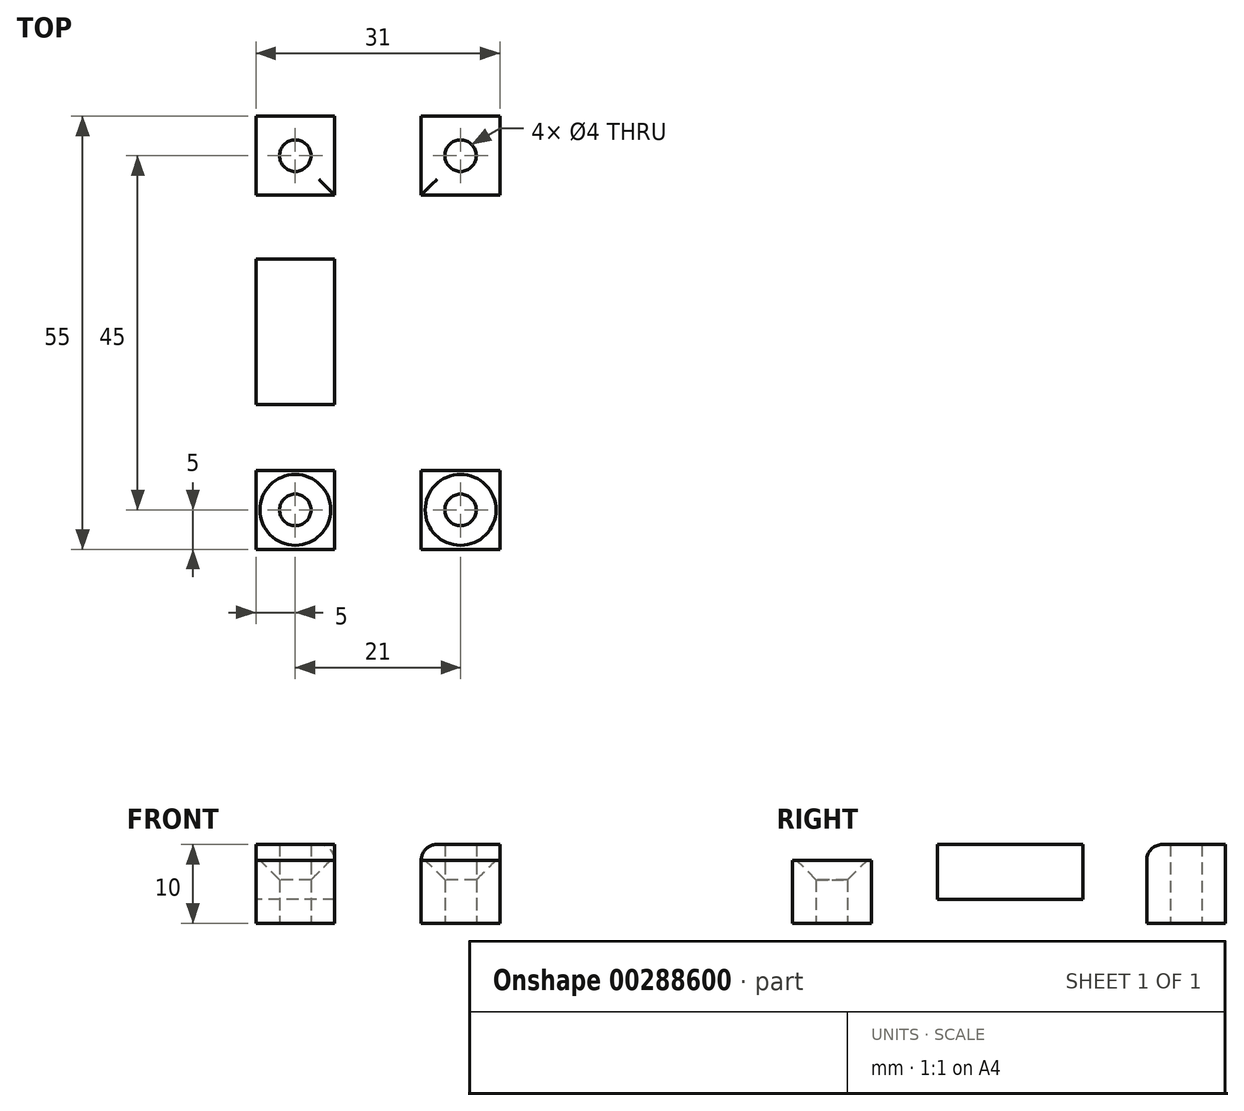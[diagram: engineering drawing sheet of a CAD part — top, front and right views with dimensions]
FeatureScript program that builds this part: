
annotation { "Feature Type Name" : "Feature", "Feature Type Description" : "" }
export const myFeature = defineFeature(function(context is Context, id is Id, definition is map)
    precondition{}
    {
        {
            var Q0;
            Q0=qCreatedBy(makeId("Top.planeOp"),FACE);
            var sketch = newSketch(context, id + "F0", { "sketchPlane" : qUnion([Q0])});
            skLineSegment(sketch, "E0.bottom", {"start": v(15.5, 27.5) * mm, "end": v(-15.5, 27.5) * mm});
            skLineSegment(sketch, "E0.top", {"start": v(15.5, -27.5) * mm, "end": v(-15.5, -27.5) * mm});
            skLineSegment(sketch, "E0.left", {"start": v(15.5, 27.5) * mm, "end": v(15.5, -27.5) * mm});
            skLineSegment(sketch, "E0.right", {"start": v(-15.5, 27.5) * mm, "end": v(-15.5, -27.5) * mm});
            skPoint(sketch, "E0.middle", {"position": v(-5.6, 0) * mm});
            skLineSegment(sketch, "E1.bottom", {"start": v(-5.5, 9.4) * mm, "end": v(-15.5, 9.4) * mm});
            skLineSegment(sketch, "E1.top", {"start": v(-5.5, -9.1) * mm, "end": v(-15.5, -9.1) * mm});
            skLineSegment(sketch, "E1.left", {"start": v(-5.5, 9.4) * mm, "end": v(-5.5, -9.1) * mm});
            skLineSegment(sketch, "E1.right", {"start": v(-15.5, 9.4) * mm, "end": v(-15.5, -9.1) * mm});
            skLineSegment(sketch, "E2.bottom", {"start": v(-15.5, 27.5) * mm, "end": v(-5.5, 27.5) * mm});
            skLineSegment(sketch, "E2.top", {"start": v(-15.5, 17.5) * mm, "end": v(-5.5, 17.5) * mm});
            skLineSegment(sketch, "E2.left", {"start": v(-15.5, 27.5) * mm, "end": v(-15.5, 17.5) * mm});
            skLineSegment(sketch, "E2.right", {"start": v(-5.5, 27.5) * mm, "end": v(-5.5, 17.5) * mm});
            skLineSegment(sketch, "E3.MirrorCS", {"start": v(15.5, 17.5) * mm, "end": v(5.5, 17.5) * mm});
            skLineSegment(sketch, "E4.MirrorCS", {"start": v(15.5, 27.5) * mm, "end": v(15.5, 17.5) * mm});
            skLineSegment(sketch, "E5.MirrorCS", {"start": v(5.5, 27.5) * mm, "end": v(5.5, 17.5) * mm});
            skLineSegment(sketch, "E6.MirrorCS", {"start": v(15.5, 27.5) * mm, "end": v(5.5, 27.5) * mm});
            skLineSegment(sketch, "E7.MirrorCS", {"start": v(15.5, -17.5) * mm, "end": v(5.5, -17.5) * mm});
            skLineSegment(sketch, "E8.MirrorCS", {"start": v(5.5, -27.5) * mm, "end": v(5.5, -17.5) * mm});
            skLineSegment(sketch, "E9.MirrorCS", {"start": v(15.5, -27.5) * mm, "end": v(15.5, 27.5) * mm});
            skLineSegment(sketch, "E10.MirrorCS", {"start": v(-15.5, -17.5) * mm, "end": v(-5.5, -17.5) * mm});
            skLineSegment(sketch, "E11.MirrorCS", {"start": v(-5.5, -27.5) * mm, "end": v(-5.5, -17.5) * mm});
            skLineSegment(sketch, "E12.MirrorCS", {"start": v(-15.5, -27.5) * mm, "end": v(-5.5, -27.5) * mm});
            skLineSegment(sketch, "E13.MirrorCS", {"start": v(-15.5, -27.5) * mm, "end": v(-15.5, -17.5) * mm});
            skSolve(sketch);
        }
        {
            var Q0;
            Q0=qCreatedBy(makeId("Top.planeOp"),FACE);
            var sketch = newSketch(context, id + "F1", { "sketchPlane" : qUnion([Q0])});
            skCircle(sketch, "E14", {"center": v(-10.5, 22.5) * mm, "radius": 2 * mm});
            skCircle(sketch, "E15.MirrorC", {"center": v(10.5, 22.5) * mm, "radius": 2 * mm});
            skCircle(sketch, "E16.MirrorC", {"center": v(-10.5, -22.5) * mm, "radius": 2 * mm});
            skCircle(sketch, "E17.MirrorC", {"center": v(10.5, -22.5) * mm, "radius": 2 * mm});
            skSolve(sketch);
        }
        {
            var Q0;
            Q0=makeQuery(id+"F0.imprint","IMPRINT",FACE,{"disambiguationData":[TD([[makeQuery(id+"F0.imprint","IMPRINT",EDGE,{"derivedFrom":sQuery(id+"F0.wireOp",EDGE,"E1.bottom")}),1.0]])]});
            var Q1;
            Q1=makeQuery(id+"F0.imprint","IMPRINT",FACE,{"disambiguationData":[TD([[makeQuery(id+"F0.imprint","IMPRINT",EDGE,{"derivedFrom":sQuery(id+"F0.wireOp",EDGE,"E0.bottom")}),1.0]])]});
            extrude(context, id + "F2", {"entities" : qUnion([Q0, Q1]), "depth" : 10 * mm});
        }
        {
            var Q0;
            Q0=makeQuery(id+"F0.imprint","IMPRINT",FACE,{"disambiguationData":[TD([[makeQuery(id+"F0.imprint","IMPRINT",EDGE,{"derivedFrom":sQuery(id+"F0.wireOp",EDGE,"E1.bottom")}),1.0]])]});
            extrude(context, id + "F3", {"entities" : qUnion([Q0]), "operationType" : NewBodyOperationType.REMOVE, "depth" : 3 * mm});
        }
        {
            var Q0;
            Q0=makeQuery(id+"F0.imprint","IMPRINT",FACE,{"disambiguationData":[TD([[makeQuery(id+"F0.imprint","IMPRINT",EDGE,{"derivedFrom":sQuery(id+"F0.wireOp",EDGE,"E2.bottom")}),-1.0]])]});
            var Q1;
            {var subQ0=sQuery(id+"F0.wireOp",EDGE,"E3.MirrorCS");Q1=makeQuery(id+"F0.imprint","IMPRINT",FACE,{"disambiguationData":[TD([[makeQuery(id+"F0.imprint","IMPRINT",EDGE,{"derivedFrom":subQ0}),-1.0]])]});}
            var Q2;
            Q2=makeQuery(id+"F0.imprint","IMPRINT",FACE,{"disambiguationData":[TD([[makeQuery(id+"F0.imprint","IMPRINT",EDGE,{"derivedFrom":sQuery(id+"F0.wireOp",EDGE,"E10.MirrorCS")}),-1.0]])]});
            var Q3;
            {var subQ0=sQuery(id+"F0.wireOp",EDGE,"E7.MirrorCS");Q3=makeQuery(id+"F0.imprint","IMPRINT",FACE,{"disambiguationData":[TD([[makeQuery(id+"F0.imprint","IMPRINT",EDGE,{"derivedFrom":subQ0}),1.0]])]});}
            extrude(context, id + "F4", {"entities" : qUnion([Q0, Q1, Q2, Q3]), "operationType" : NewBodyOperationType.ADD, "depth" : 8 * mm});
        }
        {
            var Q0;
            Q0 = qSketchRegion(id + "F1", true);
            extrude(context, id + "F5", {"entities" : qUnion([Q0]), "operationType" : NewBodyOperationType.REMOVE, "depth" : 25 * mm});
        }
        {
            var Q0;
            Q0=makeQuery(id+"F5.boolean.opBoolean","INTERSECT",EDGE,{"derivedFrom":[makeQuery(id+"F4.opExtrude","CAP_FACE",FACE,{"disambiguationData":[OSD([sQuery(id+"F0.wireOp",EDGE,"E2.bottom"),sQuery(id+"F0.wireOp",EDGE,"E2.top"),sQuery(id+"F0.wireOp",EDGE,"E2.left"),sQuery(id+"F0.wireOp",EDGE,"E2.right")])],"isStart":false}),makeQuery(id+"F5.opExtrude","SWEPT_FACE",FACE,{"disambiguationData":[OSD([sQuery(id+"F1.wireOp",EDGE,"E14")])]})]});
            var Q1;
            Q1=makeQuery(id+"F5.boolean.opBoolean","INTERSECT",EDGE,{"derivedFrom":[makeQuery(id+"F4.opExtrude","CAP_FACE",FACE,{"disambiguationData":[OSD([sQuery(id+"F0.wireOp",EDGE,"E3.MirrorCS"),sQuery(id+"F0.wireOp",EDGE,"E5.MirrorCS"),sQuery(id+"F0.wireOp",EDGE,"E6.MirrorCS"),sQuery(id+"F0.wireOp",EDGE,"E9.MirrorCS")])],"isStart":false}),makeQuery(id+"F5.opExtrude","SWEPT_FACE",FACE,{"disambiguationData":[OSD([sQuery(id+"F1.wireOp",EDGE,"E15.MirrorC")])]})]});
            var Q2;
            Q2=makeQuery(id+"F5.boolean.opBoolean","INTERSECT",EDGE,{"derivedFrom":[makeQuery(id+"F4.opExtrude","CAP_FACE",FACE,{"disambiguationData":[OSD([sQuery(id+"F0.wireOp",EDGE,"E7.MirrorCS"),sQuery(id+"F0.wireOp",EDGE,"E8.MirrorCS"),sQuery(id+"F0.wireOp",EDGE,"E0.top"),sQuery(id+"F0.wireOp",EDGE,"E9.MirrorCS")])],"isStart":false}),makeQuery(id+"F5.opExtrude","SWEPT_FACE",FACE,{"disambiguationData":[OSD([sQuery(id+"F1.wireOp",EDGE,"E17.MirrorC")])]})]});
            var Q3;
            Q3=makeQuery(id+"F5.boolean.opBoolean","INTERSECT",EDGE,{"derivedFrom":[makeQuery(id+"F4.opExtrude","CAP_FACE",FACE,{"disambiguationData":[OSD([sQuery(id+"F0.wireOp",EDGE,"E10.MirrorCS"),sQuery(id+"F0.wireOp",EDGE,"E11.MirrorCS"),sQuery(id+"F0.wireOp",EDGE,"E12.MirrorCS"),sQuery(id+"F0.wireOp",EDGE,"E13.MirrorCS")])],"isStart":false}),makeQuery(id+"F5.opExtrude","SWEPT_FACE",FACE,{"disambiguationData":[OSD([sQuery(id+"F1.wireOp",EDGE,"E16.MirrorC")])]})]});
            chamfer(context, id + "F6", {"entities" : qUnion([Q0, Q1, Q2, Q3]), "width" : 2.5 * mm, "tangentPropagation" : true});
        }
        {
            var Q0;
            Q0=makeQuery(id+"F2.opExtrude","CAP_EDGE",EDGE,{"disambiguationData":[OSD([sQuery(id+"F0.wireOp",EDGE,"E10.MirrorCS")])],"isStart":false});
            var Q1;
            Q1=makeQuery(id+"F2.opExtrude","CAP_EDGE",EDGE,{"disambiguationData":[OSD([sQuery(id+"F0.wireOp",EDGE,"E11.MirrorCS")])],"isStart":false});
            var Q2;
            Q2=makeQuery(id+"F2.opExtrude","CAP_EDGE",EDGE,{"disambiguationData":[OSD([sQuery(id+"F0.wireOp",EDGE,"E2.top")])],"isStart":false});
            var Q3;
            Q3=makeQuery(id+"F2.opExtrude","CAP_EDGE",EDGE,{"disambiguationData":[OSD([sQuery(id+"F0.wireOp",EDGE,"E2.right")])],"isStart":false});
            var Q4;
            Q4=makeQuery(id+"F2.opExtrude","CAP_EDGE",EDGE,{"disambiguationData":[OSD([sQuery(id+"F0.wireOp",EDGE,"E5.MirrorCS")])],"isStart":false});
            var Q5;
            Q5=makeQuery(id+"F2.opExtrude","CAP_EDGE",EDGE,{"disambiguationData":[OSD([sQuery(id+"F0.wireOp",EDGE,"E3.MirrorCS")])],"isStart":false});
            var Q6;
            Q6=makeQuery(id+"F2.opExtrude","CAP_EDGE",EDGE,{"disambiguationData":[OSD([sQuery(id+"F0.wireOp",EDGE,"E7.MirrorCS")])],"isStart":false});
            var Q7;
            Q7=makeQuery(id+"F2.opExtrude","CAP_EDGE",EDGE,{"disambiguationData":[OSD([sQuery(id+"F0.wireOp",EDGE,"E8.MirrorCS")])],"isStart":false});
            fillet(context, id + "F7", {"entities" : qUnion([Q0, Q1, Q2, Q3, Q4, Q5, Q6, Q7]), "radius" : 2 * mm, "tangentPropagation" : true, "allowEdgeOverflow" : false});
        }
    });
